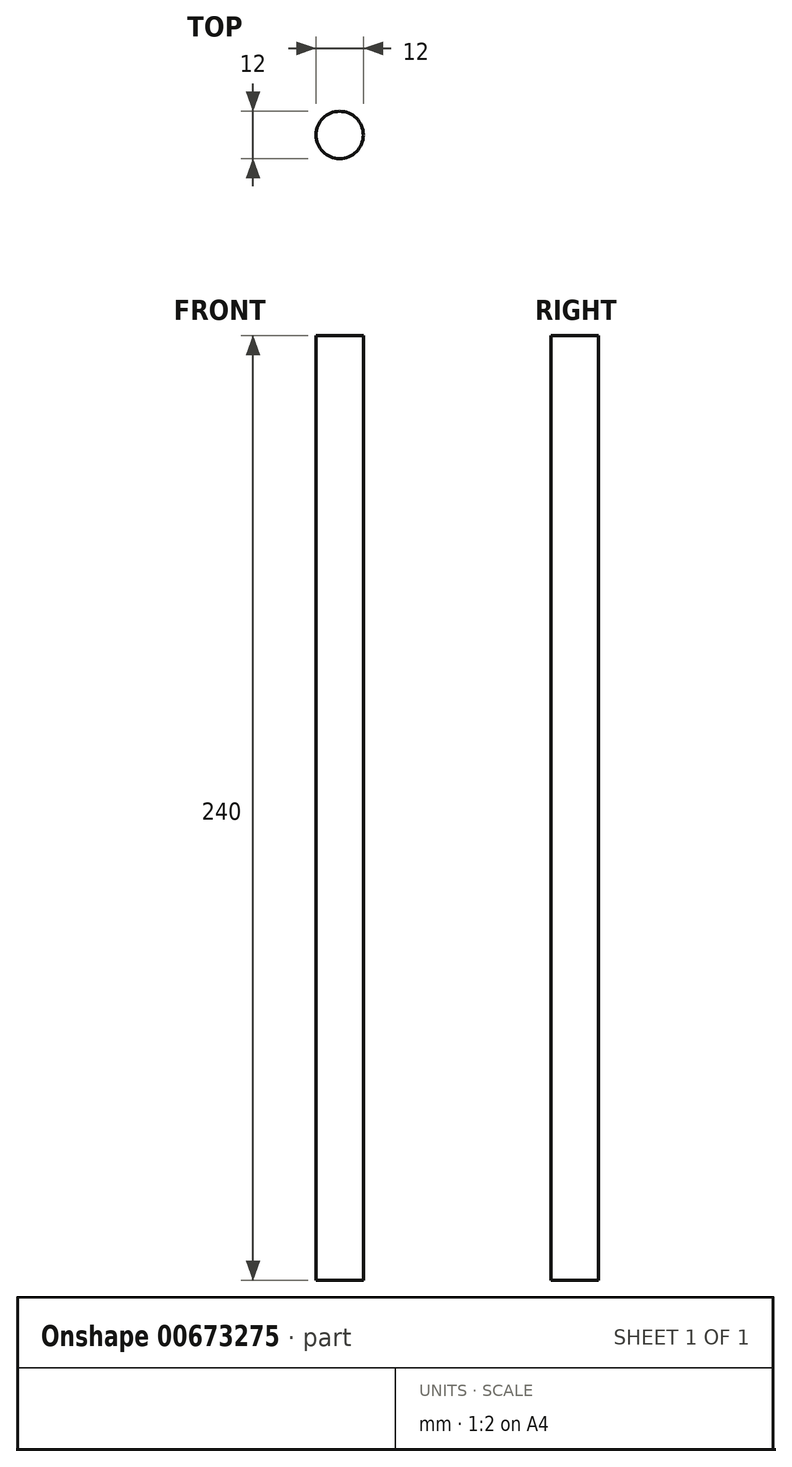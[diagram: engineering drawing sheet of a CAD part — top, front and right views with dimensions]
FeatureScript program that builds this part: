
annotation { "Feature Type Name" : "Feature", "Feature Type Description" : "" }
export const myFeature = defineFeature(function(context is Context, id is Id, definition is map)
    precondition{}
    {
        {
            var Q0;
            Q0=qCreatedBy(makeId("Top.planeOp"),FACE);
            var sketch = newSketch(context, id + "F0", { "sketchPlane" : qUnion([Q0])});
            skCircle(sketch, "E0", {"center": v(0, 0) * mm, "radius": 6 * mm});
            skSolve(sketch);
        }
        {
            var Q0;
            Q0=makeQuery(id+"F0.imprint","IMPRINT",FACE,{"disambiguationData":[TD([[makeQuery(id+"F0.imprint","IMPRINT",EDGE,{"derivedFrom":sQuery(id+"F0.wireOp",EDGE,"E0")}),1.0]])]});
            extrude(context, id + "F1", {"entities" : qUnion([Q0]), "depth" : 240 * mm, "offsetDistance" : 25 * mm});
        }
    });
